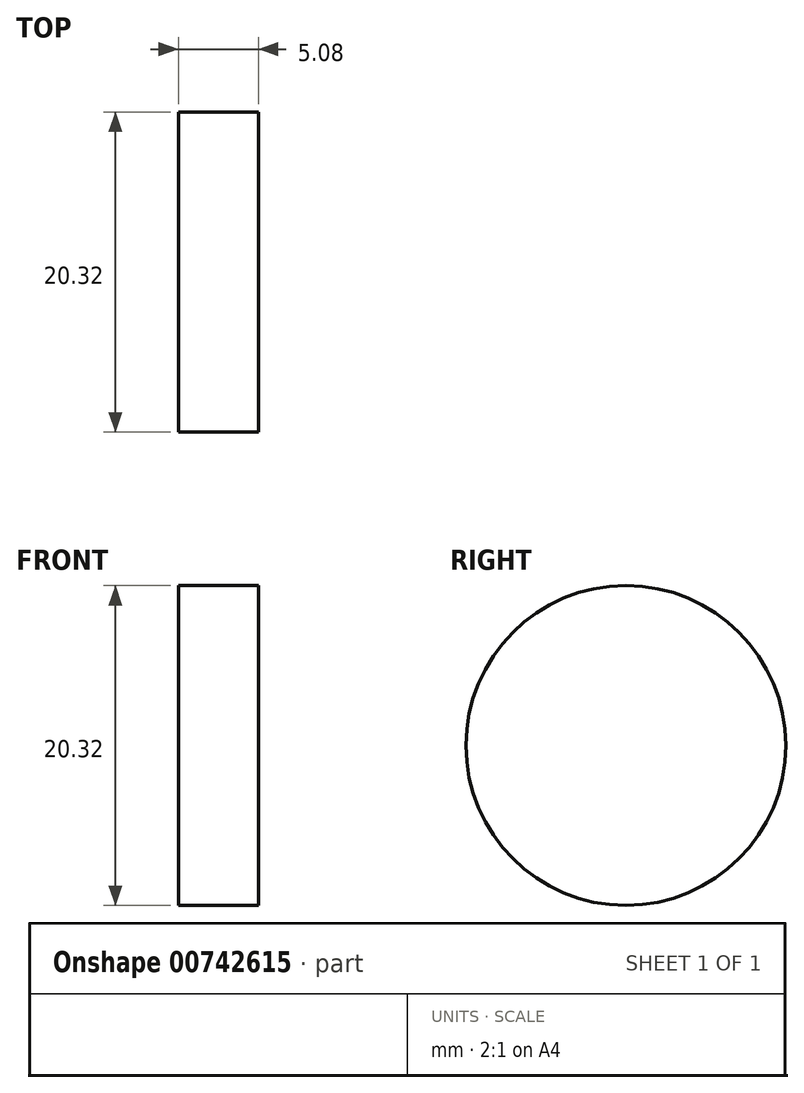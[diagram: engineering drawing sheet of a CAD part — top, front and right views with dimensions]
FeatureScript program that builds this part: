
annotation { "Feature Type Name" : "Feature", "Feature Type Description" : "" }
export const myFeature = defineFeature(function(context is Context, id is Id, definition is map)
    precondition{}
    {
        {
            var Q0;
            Q0=qCreatedBy(makeId("Right.planeOp"),FACE);
            var sketch = newSketch(context, id + "F0", { "sketchPlane" : qUnion([Q0])});
            skCircle(sketch, "E0", {"center": v(0, 0) * mm, "radius": 10.16 * mm});
            skSolve(sketch);
        }
        {
            var Q0;
            Q0 = qSketchRegion(id + "F0", true);
            extrude(context, id + "F1", {"entities" : qUnion([Q0]), "depth" : 5.08 * mm, "offsetDistance" : 25.4 * mm});
        }
    });
